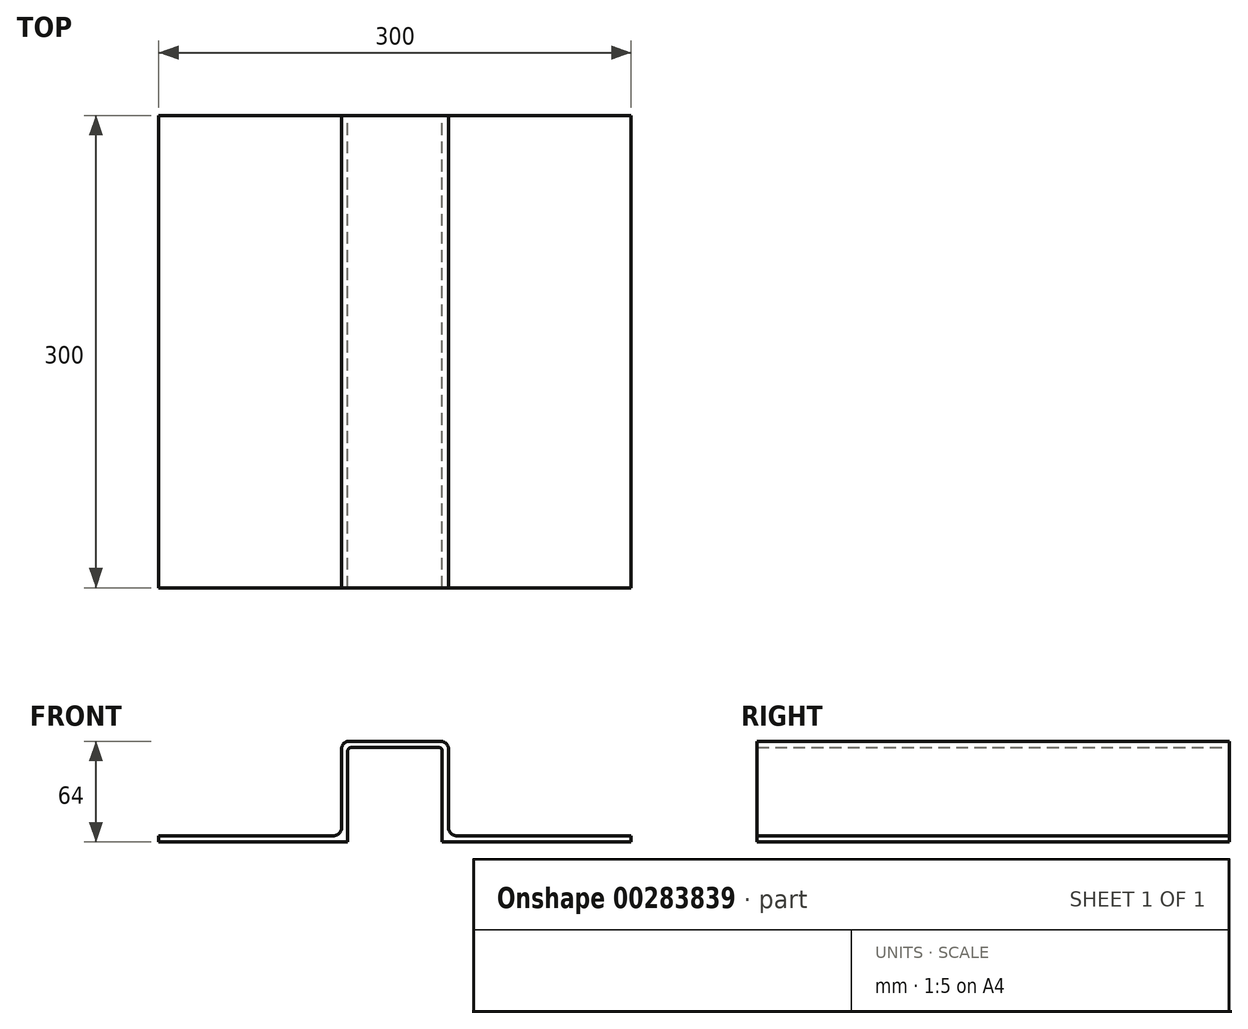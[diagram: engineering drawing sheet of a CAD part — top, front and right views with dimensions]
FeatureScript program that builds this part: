
annotation { "Feature Type Name" : "Feature", "Feature Type Description" : "" }
export const myFeature = defineFeature(function(context is Context, id is Id, definition is map)
    precondition{}
    {
        {
            var Q0;
            Q0=qCreatedBy(makeId("Front.planeOp"),FACE);
            var sketch = newSketch(context, id + "F0", { "sketchPlane" : qUnion([Q0])});
            skLineSegment(sketch, "E0", {"start": v(-150, 0) * mm, "end": v(-30, 0) * mm});
            skLineSegment(sketch, "E1", {"start": v(-30, 0) * mm, "end": v(-30, 60) * mm});
            skLineSegment(sketch, "E2", {"start": v(30, 60) * mm, "end": v(30, 0) * mm});
            skLineSegment(sketch, "E3", {"start": v(30, 0) * mm, "end": v(150, 0) * mm});
            skLineSegment(sketch, "E4", {"start": v(-30, 60) * mm, "end": v(0, 60) * mm});
            skLineSegment(sketch, "E5", {"start": v(0, 60) * mm, "end": v(30, 60) * mm});
            skLineSegment(sketch, "E6.0", {"start": v(34, 4) * mm, "end": v(150, 4) * mm});
            skLineSegment(sketch, "E6.1", {"start": v(34, 64) * mm, "end": v(34, 4) * mm});
            skLineSegment(sketch, "E6.2", {"start": v(-150, 4) * mm, "end": v(-34, 4) * mm});
            skLineSegment(sketch, "E6.3", {"start": v(-34, 4) * mm, "end": v(-34, 64) * mm});
            skLineSegment(sketch, "E6.4", {"start": v(-34, 64) * mm, "end": v(0, 64) * mm});
            skLineSegment(sketch, "E6.5", {"start": v(0, 64) * mm, "end": v(34, 64) * mm});
            skLineSegment(sketch, "E7", {"start": v(-150, 0) * mm, "end": v(-150, 4) * mm});
            skLineSegment(sketch, "E8", {"start": v(150, 0) * mm, "end": v(150, 4) * mm});
            skSolve(sketch);
        }
        {
            var Q0;
            Q0=makeQuery(id+"F0.imprint","IMPRINT",FACE,{"disambiguationData":[TD([[makeQuery(id+"F0.imprint","IMPRINT",EDGE,{"derivedFrom":sQuery(id+"F0.wireOp",EDGE,"E0")}),1.0]])]});
            extrude(context, id + "F1", {"entities" : qUnion([Q0]), "depth" : 300 * mm});
        }
        {
            var Q0;
            Q0=makeQuery(id+"F1.opExtrude","SWEPT_EDGE",EDGE,{"disambiguationData":[OSD([sQuery(id+"F0.wireOp",EDGE,"E6.2"),sQuery(id+"F0.wireOp",EDGE,"E6.3")])]});
            var Q1;
            Q1=makeQuery(id+"F1.opExtrude","SWEPT_EDGE",EDGE,{"disambiguationData":[OSD([sQuery(id+"F0.wireOp",EDGE,"E6.0"),sQuery(id+"F0.wireOp",EDGE,"E6.1")])]});
            var Q2;
            Q2=makeQuery(id+"F1.opExtrude","SWEPT_EDGE",EDGE,{"disambiguationData":[OSD([sQuery(id+"F0.wireOp",EDGE,"E6.1"),sQuery(id+"F0.wireOp",EDGE,"E6.5")])]});
            var Q3;
            Q3=makeQuery(id+"F1.opExtrude","SWEPT_EDGE",EDGE,{"disambiguationData":[OSD([sQuery(id+"F0.wireOp",EDGE,"E6.3"),sQuery(id+"F0.wireOp",EDGE,"E6.4")])]});
            fillet(context, id + "F2", {"entities" : qUnion([Q0, Q1, Q2, Q3]), "radius" : 5 * mm, "tangentPropagation" : true, "allowEdgeOverflow" : false});
        }
        {
            var Q0;
            Q0=makeQuery(id+"F1.opExtrude","SWEPT_EDGE",EDGE,{"disambiguationData":[OSD([sQuery(id+"F0.wireOp",EDGE,"E2"),sQuery(id+"F0.wireOp",EDGE,"E5")])]});
            var Q1;
            Q1=makeQuery(id+"F1.opExtrude","SWEPT_EDGE",EDGE,{"disambiguationData":[OSD([sQuery(id+"F0.wireOp",EDGE,"E1"),sQuery(id+"F0.wireOp",EDGE,"E4")])]});
            fillet(context, id + "F3", {"entities" : qUnion([Q0, Q1]), "radius" : 2 * mm, "tangentPropagation" : true, "allowEdgeOverflow" : false});
        }
    });
